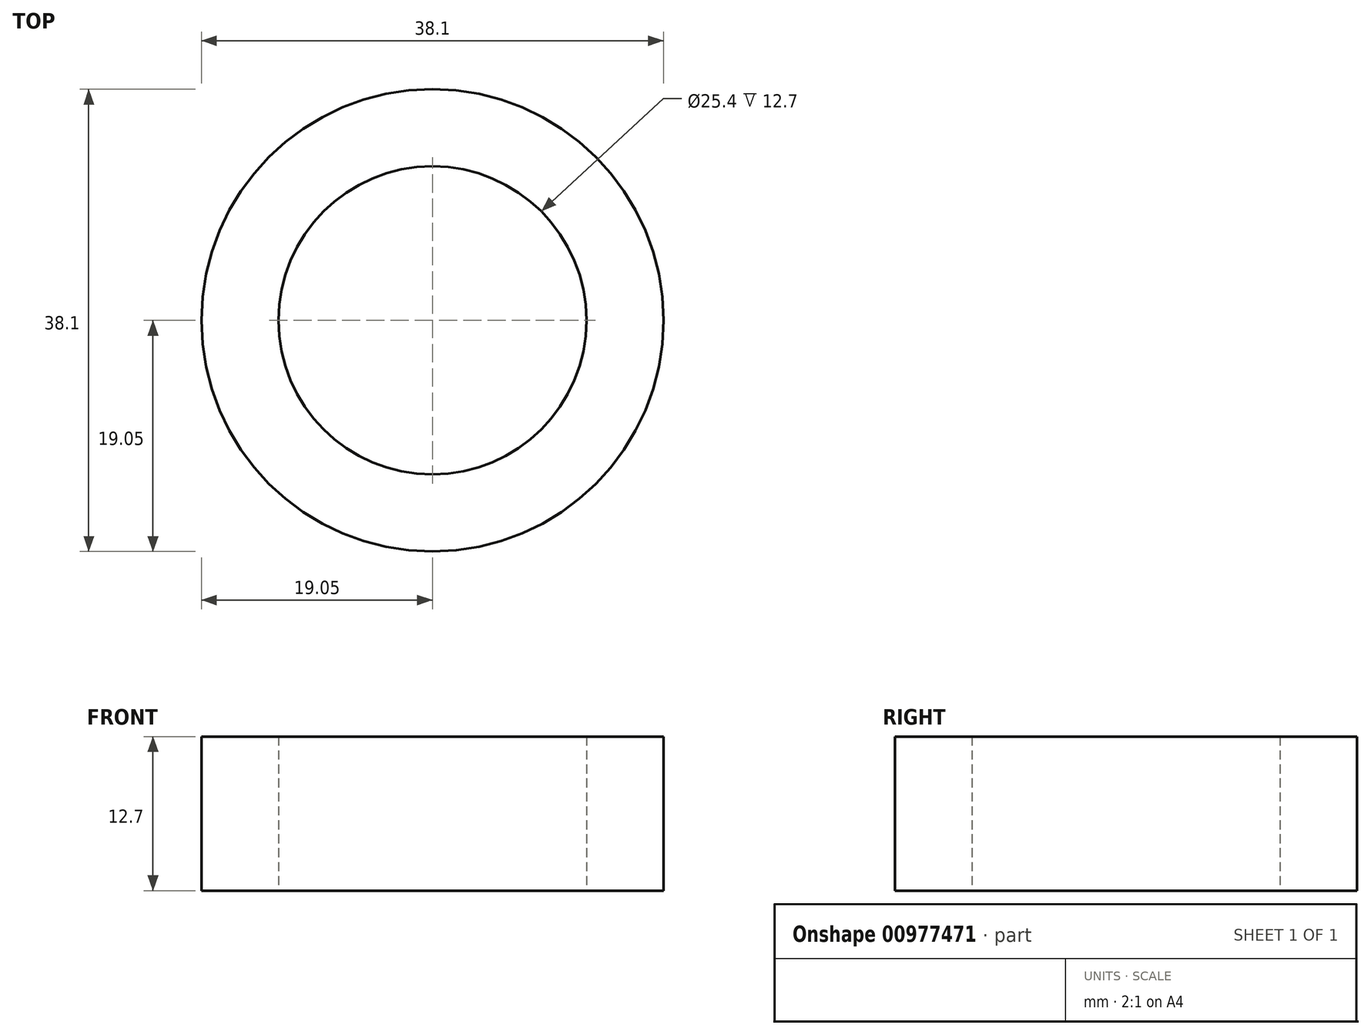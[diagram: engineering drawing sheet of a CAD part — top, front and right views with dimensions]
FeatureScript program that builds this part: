
annotation { "Feature Type Name" : "Feature", "Feature Type Description" : "" }
export const myFeature = defineFeature(function(context is Context, id is Id, definition is map)
    precondition{}
    {
        {
            var Q0;
            Q0=qCreatedBy(makeId("Top.planeOp"),FACE);
            var sketch = newSketch(context, id + "F0", { "sketchPlane" : qUnion([Q0])});
            skCircle(sketch, "E0", {"center": v(0, 0) * mm, "radius": 12.7 * mm});
            skCircle(sketch, "E1", {"center": v(0, 0) * mm, "radius": 19.05 * mm});
            skSolve(sketch);
        }
        {
            var Q0;
            Q0=makeQuery(id+"F0.imprint","IMPRINT",FACE,{"disambiguationData":[TD([[makeQuery(id+"F0.imprint","IMPRINT",EDGE,{"derivedFrom":sQuery(id+"F0.wireOp",EDGE,"E0")}),-1.0]])]});
            extrude(context, id + "F1", {"entities" : qUnion([Q0]), "depth" : 12.7 * mm, "offsetDistance" : 25.4 * mm});
        }
    });
